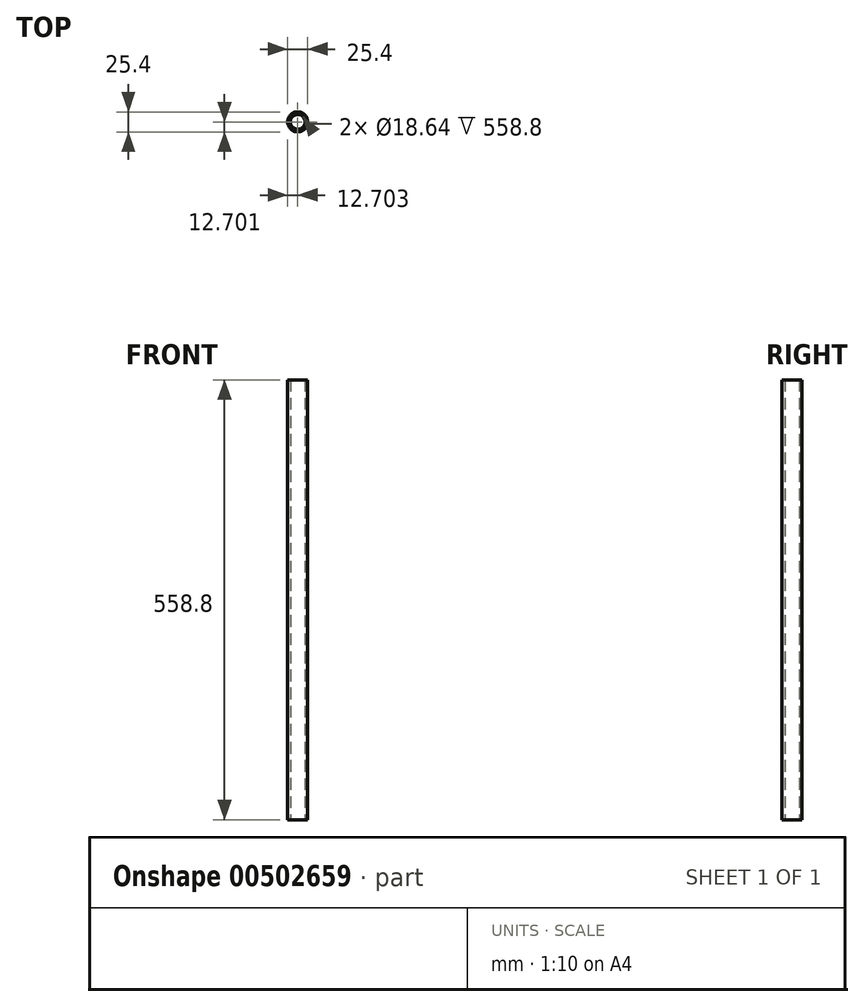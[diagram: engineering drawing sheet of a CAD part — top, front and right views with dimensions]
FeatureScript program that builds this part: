
annotation { "Feature Type Name" : "Feature", "Feature Type Description" : "" }
export const myFeature = defineFeature(function(context is Context, id is Id, definition is map)
    precondition{}
    {
        {
            var Q0;
            Q0=qCreatedBy(makeId("Top.planeOp"),FACE);
            var sketch = newSketch(context, id + "F0", { "sketchPlane" : qUnion([Q0])});
            skCircle(sketch, "E0", {"center": v(47.58, -48.34) * mm, "radius": 12.7 * mm});
            skCircle(sketch, "E1", {"center": v(47.58, -48.34) * mm, "radius": 9.32 * mm});
            skCircle(sketch, "E2", {"center": v(-58.04, -192.54) * mm, "radius": 58.48 * mm});
            skSolve(sketch);
        }
        {
            var Q0;
            Q0=makeQuery(id+"F0.imprint","IMPRINT",FACE,{"disambiguationData":[TD([[makeQuery(id+"F0.imprint","IMPRINT",EDGE,{"derivedFrom":sQuery(id+"F0.wireOp",EDGE,"E0")}),1.0]])]});
            extrude(context, id + "F1", {"entities" : qUnion([Q0]), "depth" : 558.8 * mm});
        }
    });
